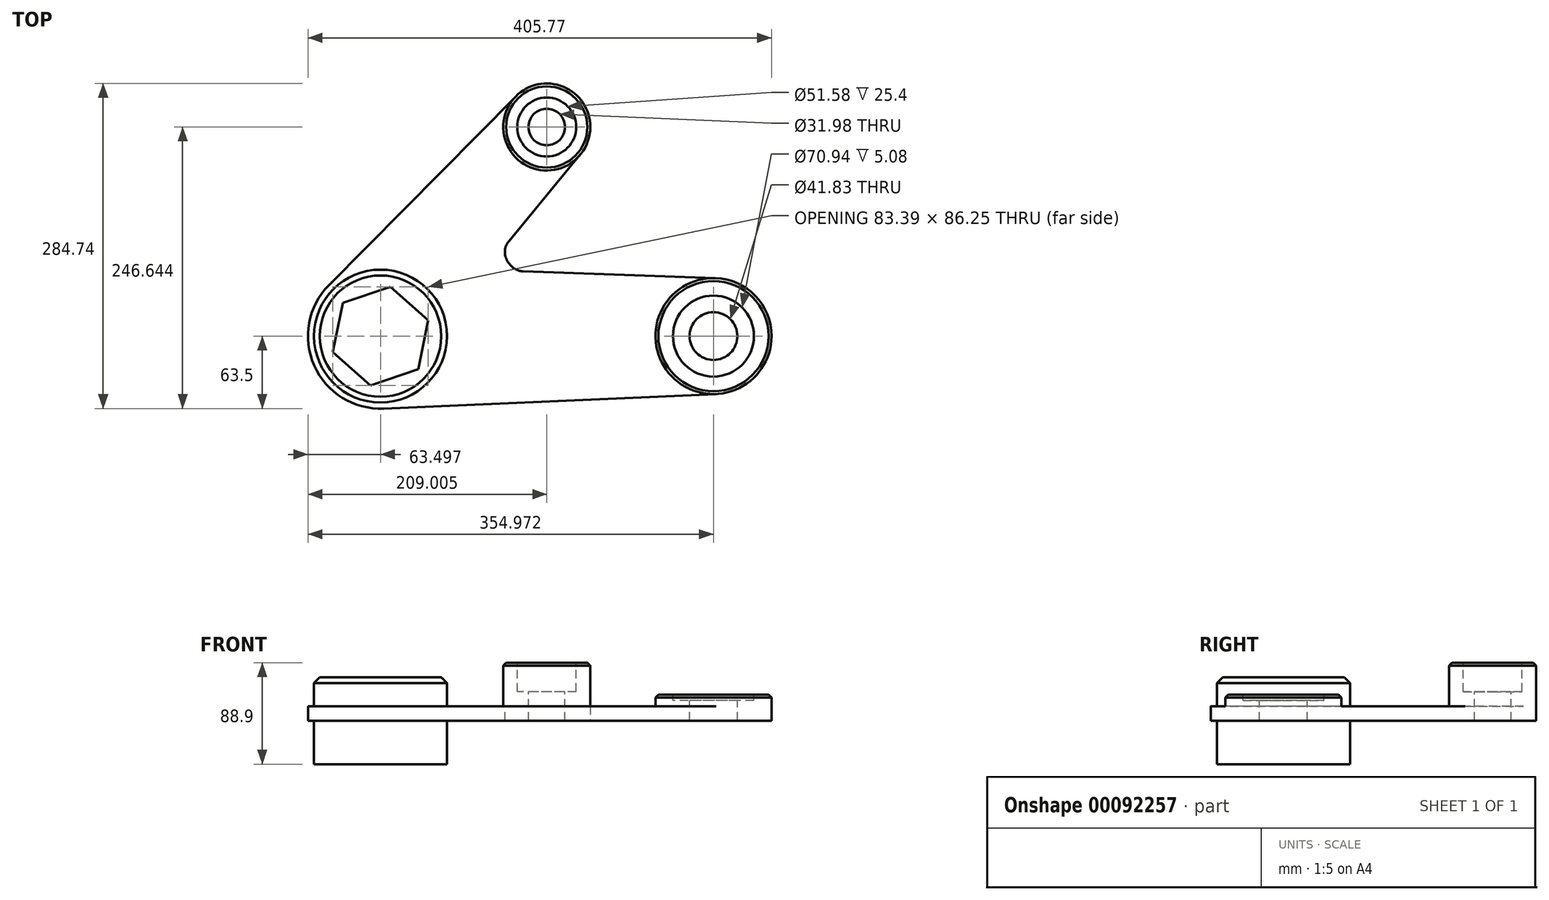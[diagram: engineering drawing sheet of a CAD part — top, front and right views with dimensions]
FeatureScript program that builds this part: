
annotation { "Feature Type Name" : "Feature", "Feature Type Description" : "" }
export const myFeature = defineFeature(function(context is Context, id is Id, definition is map)
    precondition{}
    {
        {
            var Q0;
            Q0=qCreatedBy(makeId("Top.planeOp"),FACE);
            var sketch = newSketch(context, id + "F0", { "sketchPlane" : qUnion([Q0])});
            skCircle(sketch, "E0", {"center": v(-104.33, 0) * mm, "radius": 63.5 * mm});
            skCircle(sketch, "E1", {"center": v(41.18, 183.14) * mm, "radius": 38.1 * mm});
            skCircle(sketch, "E2", {"center": v(187.14, 0) * mm, "radius": 50.8 * mm});
            skLineSegment(sketch, "E3", {"start": v(-149.47, 44.67) * mm, "end": v(14.1, 209.94) * mm});
            skPoint(sketch, "E4", {"position": v(0, 73.47) * mm});
            skLineSegment(sketch, "E5", {"start": v(70.55, 158.88) * mm, "end": v(0, 73.47) * mm});
            skPoint(sketch, "E6", {"position": v(13.85, 56.92) * mm});
            skLineSegment(sketch, "E7", {"start": v(13.85, 56.92) * mm, "end": v(188.93, 50.77) * mm});
            skLineSegment(sketch, "E8", {"start": v(0, 73.47) * mm, "end": v(13.85, 56.92) * mm});
            skLineSegment(sketch, "E9", {"start": v(-101.57, -63.44) * mm, "end": v(189.36, -50.75) * mm});
            skSolve(sketch);
        }
        {
            var Q0;
            Q0 = qSketchRegion(id + "F0", true);
            extrude(context, id + "F1", {"entities" : qUnion([Q0]), "depth" : 12.7 * mm});
        }
        {
            var Q0;
            Q0=makeQuery(id+"F1.opExtrude","CAP_FACE",FACE,{"disambiguationData":[OSD([sQuery(id+"F0.wireOp",EDGE,"E0"),sQuery(id+"F0.wireOp",EDGE,"E1"),sQuery(id+"F0.wireOp",EDGE,"E2"),sQuery(id+"F0.wireOp",EDGE,"E3"),sQuery(id+"F0.wireOp",EDGE,"E5"),sQuery(id+"F0.wireOp",EDGE,"E7"),sQuery(id+"F0.wireOp",EDGE,"E8"),sQuery(id+"F0.wireOp",EDGE,"E9")])],"isStart":false});
            var sketch = newSketch(context, id + "F2", { "sketchPlane" : qUnion([Q0])});
            skCircle(sketch, "E10", {"center": v(-104.33, 0) * mm, "radius": 58.2 * mm});
            skSolve(sketch);
        }
        {
            var Q0;
            Q0 = qSketchRegion(id + "F2", true);
            extrude(context, id + "F3", {"entities" : qUnion([Q0]), "operationType" : NewBodyOperationType.ADD, "depth" : 25.4 * mm, "hasSecondDirection" : true, "secondDirectionOppositeDirection" : true, "secondDirectionDepth" : 50.8 * mm});
        }
        {
            var Q0;
            Q0=makeQuery(id+"F3.opExtrude","CAP_EDGE",EDGE,{"disambiguationData":[OSD([sQuery(id+"F2.wireOp",EDGE,"E10")])],"isStart":false});
            chamfer(context, id + "F4", {"entities" : qUnion([Q0]), "width" : 5.08 * mm, "tangentPropagation" : true});
        }
        {
            var Q0;
            Q0=makeQuery(id+"F3.opExtrude","CAP_FACE",FACE,{"disambiguationData":[OSD([sQuery(id+"F2.wireOp",EDGE,"E10")])],"isStart":false});
            var sketch = newSketch(context, id + "F5", { "sketchPlane" : qUnion([Q0])});
            skCircle(sketch, "E11.cCircle", {"center": v(-104.33, 0) * mm, "radius": 38.1 * mm, "construction": true});
            skLineSegment(sketch, "E11.0", {"start": v(-71.33, -29.1) * mm, "end": v(-113.03, -43.13) * mm});
            skLineSegment(sketch, "E11.1", {"start": v(-113.03, -43.13) * mm, "end": v(-146.03, -14.03) * mm});
            skLineSegment(sketch, "E11.2", {"start": v(-146.03, -14.03) * mm, "end": v(-137.33, 29.1) * mm});
            skLineSegment(sketch, "E11.3", {"start": v(-137.33, 29.1) * mm, "end": v(-95.64, 43.13) * mm});
            skLineSegment(sketch, "E11.4", {"start": v(-95.64, 43.13) * mm, "end": v(-62.64, 14.03) * mm});
            skLineSegment(sketch, "E11.5", {"start": v(-62.64, 14.03) * mm, "end": v(-71.33, -29.1) * mm});
            skPoint(sketch, "E11.0.midPoint", {"position": v(-92.18, -36.11) * mm});
            skSolve(sketch);
        }
        {
            var Q0;
            Q0 = qSketchRegion(id + "F5", true);
            extrude(context, id + "F6", {"entities" : qUnion([Q0]), "operationType" : NewBodyOperationType.REMOVE, "endBound" : BoundingType.THROUGH_ALL, "oppositeDirection" : true, "depth" : 25.4 * mm});
        }
        {
            var Q0;
            Q0=makeQuery(id+"F1.opExtrude","CAP_FACE",FACE,{"disambiguationData":[OSD([sQuery(id+"F0.wireOp",EDGE,"E0"),sQuery(id+"F0.wireOp",EDGE,"E1"),sQuery(id+"F0.wireOp",EDGE,"E2"),sQuery(id+"F0.wireOp",EDGE,"E3"),sQuery(id+"F0.wireOp",EDGE,"E5"),sQuery(id+"F0.wireOp",EDGE,"E7"),sQuery(id+"F0.wireOp",EDGE,"E8"),sQuery(id+"F0.wireOp",EDGE,"E9")])],"isStart":false});
            var sketch = newSketch(context, id + "F7", { "sketchPlane" : qUnion([Q0])});
            skCircle(sketch, "E12", {"center": v(41.18, 183.14) * mm, "radius": 38.1 * mm});
            skSolve(sketch);
        }
        {
            var Q0;
            Q0 = qSketchRegion(id + "F7", true);
            extrude(context, id + "F8", {"entities" : qUnion([Q0]), "operationType" : NewBodyOperationType.ADD, "depth" : 38.1 * mm});
        }
        {
            var Q0;
            Q0=makeQuery(id+"F8.opExtrude","CAP_EDGE",EDGE,{"disambiguationData":[OSD([sQuery(id+"F7.wireOp",EDGE,"E12")])],"isStart":false});
            chamfer(context, id + "F9", {"entities" : qUnion([Q0]), "width" : 2.54 * mm, "tangentPropagation" : true});
        }
        {
            var Q0;
            Q0=makeQuery(id+"F8.opExtrude","CAP_FACE",FACE,{"disambiguationData":[OSD([sQuery(id+"F7.wireOp",EDGE,"E12")])],"isStart":false});
            var sketch = newSketch(context, id + "F10", { "sketchPlane" : qUnion([Q0])});
            skCircle(sketch, "E13", {"center": v(41.18, 183.14) * mm, "radius": 25.8 * mm});
            skSolve(sketch);
        }
        {
            var Q0;
            Q0 = qSketchRegion(id + "F10", true);
            extrude(context, id + "F11", {"entities" : qUnion([Q0]), "operationType" : NewBodyOperationType.REMOVE, "oppositeDirection" : true, "depth" : 25.4 * mm});
        }
        {
            var Q0;
            Q0=makeQuery(id+"F11.boolean.opBoolean","COPY",FACE,{"derivedFrom":makeQuery(id+"F11.opExtrude","CAP_FACE",FACE,{"disambiguationData":[OSD([sQuery(id+"F10.wireOp",EDGE,"E13")])],"isStart":false})});
            var sketch = newSketch(context, id + "F12", { "sketchPlane" : qUnion([Q0])});
            skCircle(sketch, "E14", {"center": v(41.18, 183.14) * mm, "radius": 15.99 * mm});
            skSolve(sketch);
        }
        {
            var Q0;
            Q0 = qSketchRegion(id + "F12", true);
            extrude(context, id + "F13", {"entities" : qUnion([Q0]), "operationType" : NewBodyOperationType.REMOVE, "endBound" : BoundingType.THROUGH_ALL, "oppositeDirection" : true, "depth" : 25.4 * mm});
        }
        {
            var Q0;
            Q0=makeQuery(id+"F1.opExtrude","CAP_FACE",FACE,{"disambiguationData":[OSD([sQuery(id+"F0.wireOp",EDGE,"E0"),sQuery(id+"F0.wireOp",EDGE,"E1"),sQuery(id+"F0.wireOp",EDGE,"E2"),sQuery(id+"F0.wireOp",EDGE,"E3"),sQuery(id+"F0.wireOp",EDGE,"E5"),sQuery(id+"F0.wireOp",EDGE,"E7"),sQuery(id+"F0.wireOp",EDGE,"E8"),sQuery(id+"F0.wireOp",EDGE,"E9")])],"isStart":false});
            var sketch = newSketch(context, id + "F14", { "sketchPlane" : qUnion([Q0])});
            skCircle(sketch, "E15", {"center": v(187.14, 0) * mm, "radius": 50.8 * mm});
            skSolve(sketch);
        }
        {
            var Q0;
            Q0 = qSketchRegion(id + "F14", true);
            extrude(context, id + "F15", {"entities" : qUnion([Q0]), "operationType" : NewBodyOperationType.ADD, "depth" : 10.16 * mm});
        }
        {
            var Q0;
            Q0=makeQuery(id+"F15.opExtrude","CAP_EDGE",EDGE,{"disambiguationData":[OSD([sQuery(id+"F14.wireOp",EDGE,"E15")])],"isStart":false});
            chamfer(context, id + "F16", {"entities" : qUnion([Q0]), "width" : 2.54 * mm, "tangentPropagation" : true});
        }
        {
            var Q0;
            Q0=makeQuery(id+"F15.opExtrude","CAP_FACE",FACE,{"disambiguationData":[OSD([sQuery(id+"F14.wireOp",EDGE,"E15")])],"isStart":false});
            var sketch = newSketch(context, id + "F17", { "sketchPlane" : qUnion([Q0])});
            skCircle(sketch, "E16", {"center": v(187.14, 0) * mm, "radius": 35.47 * mm});
            skSolve(sketch);
        }
        {
            var Q0;
            Q0 = qSketchRegion(id + "F17", true);
            extrude(context, id + "F18", {"entities" : qUnion([Q0]), "operationType" : NewBodyOperationType.REMOVE, "oppositeDirection" : true, "depth" : 5.08 * mm});
        }
        {
            var Q0;
            Q0=makeQuery(id+"F18.boolean.opBoolean","COPY",FACE,{"derivedFrom":makeQuery(id+"F18.opExtrude","CAP_FACE",FACE,{"disambiguationData":[OSD([sQuery(id+"F17.wireOp",EDGE,"E16")])],"isStart":false})});
            var sketch = newSketch(context, id + "F19", { "sketchPlane" : qUnion([Q0])});
            skCircle(sketch, "E17", {"center": v(187.14, 0) * mm, "radius": 20.92 * mm});
            skSolve(sketch);
        }
        {
            var Q0;
            Q0 = qSketchRegion(id + "F19", true);
            extrude(context, id + "F20", {"entities" : qUnion([Q0]), "operationType" : NewBodyOperationType.REMOVE, "endBound" : BoundingType.THROUGH_ALL, "oppositeDirection" : true, "depth" : 25.4 * mm});
        }
        {
            var Q0;
            Q0=makeQuery(id+"F1.opExtrude","SWEPT_EDGE",EDGE,{"disambiguationData":[OSD([sQuery(id+"F0.wireOp",EDGE,"E5"),sQuery(id+"F0.wireOp",EDGE,"E8")])]});
            var Q1;
            Q1=makeQuery(id+"F1.opExtrude","SWEPT_EDGE",EDGE,{"disambiguationData":[OSD([sQuery(id+"F0.wireOp",EDGE,"E7"),sQuery(id+"F0.wireOp",EDGE,"E8")])]});
            fillet(context, id + "F21", {"entities" : qUnion([Q0, Q1]), "radius" : 15.24 * mm, "tangentPropagation" : true, "allowEdgeOverflow" : false});
        }
    });
